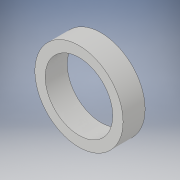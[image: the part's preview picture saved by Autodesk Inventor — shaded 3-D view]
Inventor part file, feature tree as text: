
AUTODESK INVENTOR PART (.ipt)
format: ipt  version: 2019 (Build 230136000, 136)  size: 219,648 bytes
history: native  units: mm
features: reference x4, other x3, extrude x1, sketch x1
ambient origin geometry x8: Origin, YZ Plane, XZ Plane, XY Plane, X Axis, Y Axis, Z Axis, Center Point
bodies: Body1 (feature_tree)
feature tree (9):
  extrude  "Выдавливание2"  Depth=2.0mm TaperAngle=0.0deg
  sketch  "Эскиз1"
  reference  "Ссылка1"
  reference  "Ссылка2"
  reference  "Ссылка3"
  reference  "Ссылка4"
  other  "<userpath>\Documents\GitHub\Tesla_coil_V1\3dModels\TeslaCoil.iam"
  other  "TeslaCoil.iam"
  other  "BottomBox:1"
